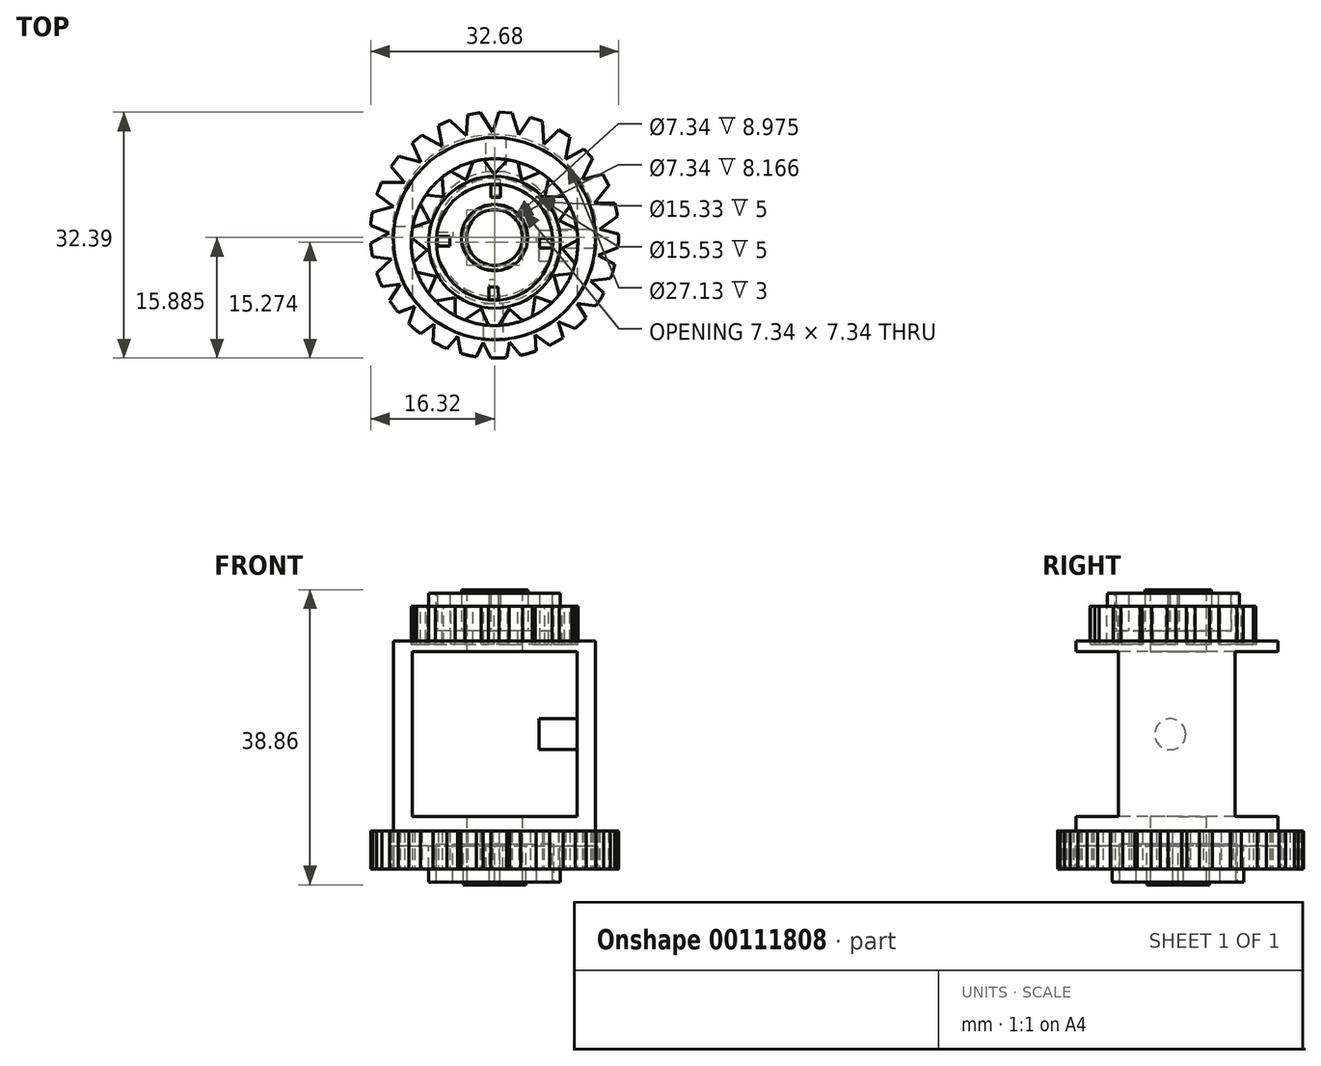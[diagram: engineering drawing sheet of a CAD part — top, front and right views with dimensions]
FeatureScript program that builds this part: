
annotation { "Feature Type Name" : "Feature", "Feature Type Description" : "" }
export const myFeature = defineFeature(function(context is Context, id is Id, definition is map)
    precondition{}
    {
        {
            var Q0;
            Q0=qCreatedBy(makeId("Top.planeOp"),FACE);
            var sketch = newSketch(context, id + "F0", { "sketchPlane" : qUnion([Q0])});
            skCircle(sketch, "E0", {"center": v(0, -2.17) * mm, "radius": 16.36 * mm});
            skSolve(sketch);
        }
        {
            var Q0;
            Q0=makeQuery(id+"F0.imprint","IMPRINT",FACE,{"disambiguationData":[TD([[makeQuery(id+"F0.imprint","IMPRINT",EDGE,{"derivedFrom":sQuery(id+"F0.wireOp",EDGE,"E0")}),1.0]])]});
            extrude(context, id + "F1", {"entities" : qUnion([Q0]), "oppositeDirection" : true, "depth" : 5 * mm});
        }
        {
            var Q0;
            Q0=qCreatedBy(makeId("Top.planeOp"),FACE);
            var sketch = newSketch(context, id + "F2", { "sketchPlane" : qUnion([Q0])});
            skCircle(sketch, "E1", {"center": v(0, -2.82) * mm, "radius": 13.3 * mm});
            skSolve(sketch);
        }
        {
            var Q0;
            Q0=makeQuery(id+"F2.imprint","IMPRINT",FACE,{"disambiguationData":[TD([[makeQuery(id+"F2.imprint","IMPRINT",EDGE,{"derivedFrom":sQuery(id+"F2.wireOp",EDGE,"E1")}),1.0]])]});
            extrude(context, id + "F3", {"entities" : qUnion([Q0]), "operationType" : NewBodyOperationType.ADD, "depth" : 25 * mm});
        }
        {
            var Q0;
            Q0=qCreatedBy(makeId("Top.planeOp"),FACE);
            var sketch = newSketch(context, id + "F4", { "sketchPlane" : qUnion([Q0])});
            skCircle(sketch, "E2", {"center": v(0, -3.26) * mm, "radius": 10.98 * mm});
            skSolve(sketch);
        }
        {
            var Q0;
            Q0 = qSketchRegion(id + "F4", true);
            extrude(context, id + "F5", {"entities" : qUnion([Q0]), "operationType" : NewBodyOperationType.ADD, "depth" : 29.59 * mm});
        }
        {
            var Q0;
            Q0=qCreatedBy(makeId("Front.planeOp"),FACE);
            var sketch = newSketch(context, id + "F6", { "sketchPlane" : qUnion([Q0])});
            skCircle(sketch, "E3.cCircle", {"center": v(0, 12.73) * mm, "radius": 10.86 * mm, "construction": true});
            skLineSegment(sketch, "E3.0", {"start": v(-10.86, 1.87) * mm, "end": v(-10.86, 23.59) * mm});
            skLineSegment(sketch, "E3.1", {"start": v(-10.86, 23.59) * mm, "end": v(10.86, 23.59) * mm});
            skLineSegment(sketch, "E3.2", {"start": v(10.86, 23.59) * mm, "end": v(10.86, 1.87) * mm});
            skLineSegment(sketch, "E3.3", {"start": v(10.86, 1.87) * mm, "end": v(-10.86, 1.87) * mm});
            skPoint(sketch, "E3.0.midPoint", {"position": v(-10.86, 12.73) * mm});
            skSolve(sketch);
        }
        {
            var Q0;
            Q0 = qSketchRegion(id + "F6", true);
            extrude(context, id + "F7", {"entities" : qUnion([Q0]), "operationType" : NewBodyOperationType.REMOVE, "oppositeDirection" : true, "depth" : 25 * mm});
        }
        {
            var Q0;
            Q0 = qSketchRegion(id + "F6", true);
            extrude(context, id + "F8", {"entities" : qUnion([Q0]), "operationType" : NewBodyOperationType.REMOVE, "depth" : 25.34 * mm});
        }
        {
            var Q0;
            Q0=qCreatedBy(makeId("Top.planeOp"),FACE);
            var sketch = newSketch(context, id + "F9", { "sketchPlane" : qUnion([Q0])});
            skCircle(sketch, "E4", {"center": v(0, -2.64) * mm, "radius": 3.67 * mm});
            skSolve(sketch);
        }
        {
            var Q0;
            Q0 = qSketchRegion(id + "F9", true);
            extrude(context, id + "F10", {"entities" : qUnion([Q0]), "operationType" : NewBodyOperationType.REMOVE, "depth" : 40.28 * mm});
        }
        {
            var Q0;
            Q0 = qSketchRegion(id + "F9", true);
            extrude(context, id + "F11", {"entities" : qUnion([Q0]), "operationType" : NewBodyOperationType.REMOVE, "oppositeDirection" : true, "depth" : 25 * mm});
        }
        {
            var Q0;
            Q0=makeQuery(id+"F5.opExtrude","CAP_FACE",FACE,{"disambiguationData":[OSD([sQuery(id+"F4.wireOp",EDGE,"E2")])],"isStart":false});
            var sketch = newSketch(context, id + "F12", { "sketchPlane" : qUnion([Q0])});
            skCircle(sketch, "E5", {"center": v(0, -3.26) * mm, "radius": 8.68 * mm});
            skSolve(sketch);
        }
        {
            var Q0;
            Q0=makeQuery(id+"F12.imprint","IMPRINT",FACE,{"disambiguationData":[TD([[makeQuery(id+"F12.imprint","IMPRINT",EDGE,{"derivedFrom":sQuery(id+"F12.wireOp",EDGE,"E5")}),1.0]])]});
            var sketch = newSketch(context, id + "F13", { "sketchPlane" : qUnion([Q0])});
            skCircle(sketch, "E6", {"center": v(0, -2.72) * mm, "radius": 3.88 * mm});
            skSolve(sketch);
        }
        {
            var Q0;
            Q0 = qSketchRegion(id + "F13", true);
            var Q1;
            Q1=makeQuery(id+"F12.imprint","IMPRINT",FACE,{"disambiguationData":[TD([[makeQuery(id+"F12.imprint","IMPRINT",EDGE,{"derivedFrom":sQuery(id+"F12.wireOp",EDGE,"E5")}),1.0]])]});
            extrude(context, id + "F14", {"entities" : qUnion([Q0, Q1]), "operationType" : NewBodyOperationType.ADD, "depth" : 1.74 * mm});
        }
        {
            var Q0;
            Q0=makeQuery(id+"F14.boolean.opBoolean","MERGE",FACE,{"derivedFrom":[makeQuery(id+"F14.opExtrude","CAP_FACE",FACE,{"disambiguationData":[OSD([sQuery(id+"F4.wireOp",EDGE,"E2"),sQuery(id+"F9.wireOp",EDGE,"E4"),sQuery(id+"F12.wireOp",EDGE,"E5")])],"isStart":false}),makeQuery(id+"F14.opExtrude","CAP_FACE",FACE,{"disambiguationData":[OSD([sQuery(id+"F13.wireOp",EDGE,"E6")])],"isStart":false})]});
            var sketch = newSketch(context, id + "F15", { "sketchPlane" : qUnion([Q0])});
            skCircle(sketch, "E7", {"center": v(0, -3.26) * mm, "radius": 7.67 * mm});
            skSolve(sketch);
        }
        {
            var Q0;
            Q0 = qSketchRegion(id + "F15", true);
            extrude(context, id + "F16", {"entities" : qUnion([Q0]), "operationType" : NewBodyOperationType.REMOVE, "oppositeDirection" : true, "depth" : 5 * mm});
        }
        {
            var Q0;
            Q0=makeQuery(id+"F16.boolean.opBoolean","COPY",FACE,{"derivedFrom":makeQuery(id+"F16.opExtrude","CAP_FACE",FACE,{"disambiguationData":[OSD([sQuery(id+"F15.wireOp",EDGE,"E7")])],"isStart":false})});
            var sketch = newSketch(context, id + "F17", { "sketchPlane" : qUnion([Q0])});
            skCircle(sketch, "E8", {"center": v(0, -2.64) * mm, "radius": 4.38 * mm});
            skSolve(sketch);
        }
        {
            var Q0;
            Q0 = qSketchRegion(id + "F17", true);
            extrude(context, id + "F18", {"entities" : qUnion([Q0]), "operationType" : NewBodyOperationType.ADD, "depth" : 5.43 * mm});
        }
        {
            var Q0;
            Q0 = qSketchRegion(id + "F9", true);
            extrude(context, id + "F19", {"entities" : qUnion([Q0]), "operationType" : NewBodyOperationType.REMOVE, "depth" : 40.72 * mm});
        }
        {
            var Q0;
            Q0=makeQuery(id+"F5.opExtrude","CAP_FACE",FACE,{"disambiguationData":[OSD([sQuery(id+"F4.wireOp",EDGE,"E2")])],"isStart":false});
            var sketch = newSketch(context, id + "F20", { "sketchPlane" : qUnion([Q0])});
            skLineSegment(sketch, "E9", {"start": v(-5.2, -10.2) * mm, "end": v(-5.2, -12.92) * mm});
            skLineSegment(sketch, "E10", {"start": v(-5.2, -12.92) * mm, "end": v(-3.94, -13.5) * mm});
            skLineSegment(sketch, "E11", {"start": v(-3.94, -13.5) * mm, "end": v(-1.46, -11.81) * mm});
            skLineSegment(sketch, "E12", {"start": v(-5.2, -10.2) * mm, "end": v(-1.46, -11.81) * mm});
            skLineSegment(sketch, "E13.1.0", {"start": v(-0.82, -14.2) * mm, "end": v(0.57, -14.22) * mm});
            skLineSegment(sketch, "E13.1.1", {"start": v(-1.93, -11.72) * mm, "end": v(-0.82, -14.2) * mm});
            skLineSegment(sketch, "E13.1.2", {"start": v(-1.93, -11.72) * mm, "end": v(2.14, -11.67) * mm});
            skLineSegment(sketch, "E13.1.3", {"start": v(0.57, -14.22) * mm, "end": v(2.14, -11.67) * mm});
            skLineSegment(sketch, "E13.2.0", {"start": v(3.7, -13.6) * mm, "end": v(4.98, -13.04) * mm});
            skLineSegment(sketch, "E13.2.1", {"start": v(1.68, -11.77) * mm, "end": v(3.7, -13.6) * mm});
            skLineSegment(sketch, "E13.2.2", {"start": v(1.68, -11.77) * mm, "end": v(5.38, -10.07) * mm});
            skLineSegment(sketch, "E13.2.3", {"start": v(4.98, -13.04) * mm, "end": v(5.38, -10.07) * mm});
            skLineSegment(sketch, "E13.3.0", {"start": v(7.59, -11.2) * mm, "end": v(8.53, -10.17) * mm});
            skLineSegment(sketch, "E13.3.1", {"start": v(5, -10.35) * mm, "end": v(7.59, -11.2) * mm});
            skLineSegment(sketch, "E13.3.2", {"start": v(5, -10.35) * mm, "end": v(7.69, -7.29) * mm});
            skLineSegment(sketch, "E13.3.3", {"start": v(8.53, -10.17) * mm, "end": v(7.69, -7.29) * mm});
            skLineSegment(sketch, "E13.4.0", {"start": v(10.16, -7.42) * mm, "end": v(10.6, -6.1) * mm});
            skLineSegment(sketch, "E13.4.1", {"start": v(7.45, -7.7) * mm, "end": v(10.16, -7.42) * mm});
            skLineSegment(sketch, "E13.4.2", {"start": v(7.45, -7.7) * mm, "end": v(8.66, -3.82) * mm});
            skLineSegment(sketch, "E13.4.3", {"start": v(10.6, -6.1) * mm, "end": v(8.66, -3.82) * mm});
            skLineSegment(sketch, "E13.5.0", {"start": v(10.97, -2.93) * mm, "end": v(10.85, -1.55) * mm});
            skLineSegment(sketch, "E13.5.1", {"start": v(8.62, -4.29) * mm, "end": v(10.97, -2.93) * mm});
            skLineSegment(sketch, "E13.5.2", {"start": v(8.62, -4.29) * mm, "end": v(8.14, -0.24) * mm});
            skLineSegment(sketch, "E13.5.3", {"start": v(10.85, -1.55) * mm, "end": v(8.14, -0.24) * mm});
            skLineSegment(sketch, "E13.6.0", {"start": v(9.9, 1.5) * mm, "end": v(9.21, 2.72) * mm});
            skLineSegment(sketch, "E13.6.1", {"start": v(8.3, -0.7) * mm, "end": v(9.9, 1.5) * mm});
            skLineSegment(sketch, "E13.6.2", {"start": v(8.3, -0.7) * mm, "end": v(6.21, 2.8) * mm});
            skLineSegment(sketch, "E13.6.3", {"start": v(9.21, 2.72) * mm, "end": v(6.21, 2.8) * mm});
            skLineSegment(sketch, "E13.7.0", {"start": v(7.1, 5.12) * mm, "end": v(5.99, 5.95) * mm});
            skLineSegment(sketch, "E13.7.1", {"start": v(6.53, 2.46) * mm, "end": v(7.1, 5.12) * mm});
            skLineSegment(sketch, "E13.7.2", {"start": v(6.53, 2.46) * mm, "end": v(3.2, 4.8) * mm});
            skLineSegment(sketch, "E13.7.3", {"start": v(5.99, 5.95) * mm, "end": v(3.2, 4.8) * mm});
            skLineSegment(sketch, "E13.8.0", {"start": v(3.08, 7.28) * mm, "end": v(1.73, 7.59) * mm});
            skLineSegment(sketch, "E13.8.1", {"start": v(3.65, 4.62) * mm, "end": v(3.08, 7.28) * mm});
            skLineSegment(sketch, "E13.8.2", {"start": v(3.65, 4.62) * mm, "end": v(-0.35, 5.42) * mm});
            skLineSegment(sketch, "E13.8.3", {"start": v(1.73, 7.59) * mm, "end": v(-0.35, 5.42) * mm});
            skLineSegment(sketch, "E13.9.0", {"start": v(-1.47, 7.62) * mm, "end": v(-2.83, 7.35) * mm});
            skLineSegment(sketch, "E13.9.1", {"start": v(0.13, 5.42) * mm, "end": v(-1.47, 7.62) * mm});
            skLineSegment(sketch, "E13.9.2", {"start": v(0.13, 5.42) * mm, "end": v(-3.85, 4.53) * mm});
            skLineSegment(sketch, "E13.9.3", {"start": v(-2.83, 7.35) * mm, "end": v(-3.85, 4.53) * mm});
            skLineSegment(sketch, "E13.10.0", {"start": v(-5.77, 6.08) * mm, "end": v(-6.9, 5.28) * mm});
            skLineSegment(sketch, "E13.10.1", {"start": v(-3.41, 4.72) * mm, "end": v(-5.77, 6.08) * mm});
            skLineSegment(sketch, "E13.10.2", {"start": v(-3.41, 4.72) * mm, "end": v(-6.68, 2.29) * mm});
            skLineSegment(sketch, "E13.10.3", {"start": v(-6.9, 5.28) * mm, "end": v(-6.68, 2.29) * mm});
            skLineSegment(sketch, "E13.11.0", {"start": v(-9.07, 2.93) * mm, "end": v(-9.78, 1.74) * mm});
            skLineSegment(sketch, "E13.11.1", {"start": v(-6.36, 2.65) * mm, "end": v(-9.07, 2.93) * mm});
            skLineSegment(sketch, "E13.11.2", {"start": v(-6.36, 2.65) * mm, "end": v(-8.36, -0.9) * mm});
            skLineSegment(sketch, "E13.11.3", {"start": v(-9.78, 1.74) * mm, "end": v(-8.36, -0.9) * mm});
            skLineSegment(sketch, "E13.12.0", {"start": v(-10.8, -1.3) * mm, "end": v(-10.96, -2.67) * mm});
            skLineSegment(sketch, "E13.12.1", {"start": v(-8.21, -0.45) * mm, "end": v(-10.8, -1.3) * mm});
            skLineSegment(sketch, "E13.12.2", {"start": v(-8.21, -0.45) * mm, "end": v(-8.59, -4.5) * mm});
            skLineSegment(sketch, "E13.12.3", {"start": v(-10.96, -2.67) * mm, "end": v(-8.59, -4.5) * mm});
            skLineSegment(sketch, "E13.13.0", {"start": v(-10.67, -5.86) * mm, "end": v(-10.25, -7.18) * mm});
            skLineSegment(sketch, "E13.13.1", {"start": v(-8.64, -4.04) * mm, "end": v(-10.67, -5.86) * mm});
            skLineSegment(sketch, "E13.13.2", {"start": v(-8.64, -4.04) * mm, "end": v(-7.34, -7.9) * mm});
            skLineSegment(sketch, "E13.13.3", {"start": v(-10.25, -7.18) * mm, "end": v(-7.34, -7.9) * mm});
            skLineSegment(sketch, "E13.14.0", {"start": v(-8.69, -9.97) * mm, "end": v(-7.77, -11.01) * mm});
            skLineSegment(sketch, "E13.14.1", {"start": v(-7.58, -7.49) * mm, "end": v(-8.69, -9.97) * mm});
            skLineSegment(sketch, "E13.14.2", {"start": v(-7.58, -7.49) * mm, "end": v(-4.82, -10.48) * mm});
            skLineSegment(sketch, "E13.14.3", {"start": v(-7.77, -11.01) * mm, "end": v(-4.82, -10.48) * mm});
            skPoint(sketch, "E13.center", {"position": v(0, -3.26) * mm});
            skSolve(sketch);
        }
        {
            var Q0;
            {var subQ0=sQuery(id+"F20.wireOp",EDGE,"E13.11.3");var subQ3=sQuery(id+"F20.wireOp",EDGE,"E13.12.1");var subQ4=makeQuery(id+"F20.imprint","INTERSECT",VERTEX,{"derivedFrom":[subQ0,subQ3]});Q0=makeQuery(id+"F20.imprint","IMPRINT",FACE,{"disambiguationData":[TD([[makeQuery(id+"F20.imprint","IMPRINT",EDGE,{"disambiguationData":[TD([[subQ4,1.0]])],"derivedFrom":subQ0}),-1.0]])]});}
            var Q1;
            {var subQ0=sQuery(id+"F20.wireOp",EDGE,"E13.12.3");var subQ3=sQuery(id+"F20.wireOp",EDGE,"E13.13.1");var subQ4=makeQuery(id+"F20.imprint","INTERSECT",VERTEX,{"derivedFrom":[subQ0,subQ3]});Q1=makeQuery(id+"F20.imprint","IMPRINT",FACE,{"disambiguationData":[TD([[makeQuery(id+"F20.imprint","IMPRINT",EDGE,{"disambiguationData":[TD([[subQ4,1.0]])],"derivedFrom":subQ0}),-1.0]])]});}
            var Q2;
            {var subQ0=sQuery(id+"F20.wireOp",EDGE,"E13.13.3");var subQ3=sQuery(id+"F20.wireOp",EDGE,"E13.14.1");var subQ4=makeQuery(id+"F20.imprint","INTERSECT",VERTEX,{"derivedFrom":[subQ0,subQ3]});Q2=makeQuery(id+"F20.imprint","IMPRINT",FACE,{"disambiguationData":[TD([[makeQuery(id+"F20.imprint","IMPRINT",EDGE,{"disambiguationData":[TD([[subQ4,1.0]])],"derivedFrom":subQ0}),-1.0]])]});}
            var Q3;
            {var subQ0=sQuery(id+"F20.wireOp",EDGE,"E11");var subQ3=sQuery(id+"F20.wireOp",EDGE,"E13.1.1");var subQ4=makeQuery(id+"F20.imprint","INTERSECT",VERTEX,{"derivedFrom":[subQ0,subQ3]});Q3=makeQuery(id+"F20.imprint","IMPRINT",FACE,{"disambiguationData":[TD([[makeQuery(id+"F20.imprint","IMPRINT",EDGE,{"disambiguationData":[TD([[subQ4,1.0]])],"derivedFrom":subQ0}),-1.0]])]});}
            var Q4;
            {var subQ0=sQuery(id+"F20.wireOp",EDGE,"E9");var subQ3=sQuery(id+"F20.wireOp",EDGE,"E13.14.3");var subQ4=makeQuery(id+"F20.imprint","INTERSECT",VERTEX,{"derivedFrom":[subQ0,subQ3]});Q4=makeQuery(id+"F20.imprint","IMPRINT",FACE,{"disambiguationData":[TD([[makeQuery(id+"F20.imprint","IMPRINT",EDGE,{"disambiguationData":[TD([[subQ4,-1.0]])],"derivedFrom":subQ0}),-1.0]])]});}
            var Q5;
            {var subQ0=sQuery(id+"F20.wireOp",EDGE,"E13.1.3");var subQ3=sQuery(id+"F20.wireOp",EDGE,"E13.2.1");var subQ4=makeQuery(id+"F20.imprint","INTERSECT",VERTEX,{"derivedFrom":[subQ0,subQ3]});Q5=makeQuery(id+"F20.imprint","IMPRINT",FACE,{"disambiguationData":[TD([[makeQuery(id+"F20.imprint","IMPRINT",EDGE,{"disambiguationData":[TD([[subQ4,1.0]])],"derivedFrom":subQ0}),-1.0]])]});}
            var Q6;
            {var subQ0=sQuery(id+"F20.wireOp",EDGE,"E13.2.3");var subQ3=sQuery(id+"F20.wireOp",EDGE,"E13.3.1");var subQ4=makeQuery(id+"F20.imprint","INTERSECT",VERTEX,{"derivedFrom":[subQ0,subQ3]});Q6=makeQuery(id+"F20.imprint","IMPRINT",FACE,{"disambiguationData":[TD([[makeQuery(id+"F20.imprint","IMPRINT",EDGE,{"disambiguationData":[TD([[subQ4,1.0]])],"derivedFrom":subQ0}),-1.0]])]});}
            var Q7;
            {var subQ0=sQuery(id+"F20.wireOp",EDGE,"E13.3.3");var subQ3=sQuery(id+"F20.wireOp",EDGE,"E13.4.1");var subQ4=makeQuery(id+"F20.imprint","INTERSECT",VERTEX,{"derivedFrom":[subQ0,subQ3]});Q7=makeQuery(id+"F20.imprint","IMPRINT",FACE,{"disambiguationData":[TD([[makeQuery(id+"F20.imprint","IMPRINT",EDGE,{"disambiguationData":[TD([[subQ4,1.0]])],"derivedFrom":subQ0}),-1.0]])]});}
            var Q8;
            {var subQ0=sQuery(id+"F20.wireOp",EDGE,"E13.4.3");var subQ3=sQuery(id+"F20.wireOp",EDGE,"E13.5.1");var subQ4=makeQuery(id+"F20.imprint","INTERSECT",VERTEX,{"derivedFrom":[subQ0,subQ3]});Q8=makeQuery(id+"F20.imprint","IMPRINT",FACE,{"disambiguationData":[TD([[makeQuery(id+"F20.imprint","IMPRINT",EDGE,{"disambiguationData":[TD([[subQ4,1.0]])],"derivedFrom":subQ0}),-1.0]])]});}
            var Q9;
            {var subQ0=sQuery(id+"F20.wireOp",EDGE,"E13.5.3");var subQ3=sQuery(id+"F20.wireOp",EDGE,"E13.6.1");var subQ4=makeQuery(id+"F20.imprint","INTERSECT",VERTEX,{"derivedFrom":[subQ0,subQ3]});Q9=makeQuery(id+"F20.imprint","IMPRINT",FACE,{"disambiguationData":[TD([[makeQuery(id+"F20.imprint","IMPRINT",EDGE,{"disambiguationData":[TD([[subQ4,1.0]])],"derivedFrom":subQ0}),-1.0]])]});}
            var Q10;
            {var subQ0=sQuery(id+"F20.wireOp",EDGE,"E13.6.3");var subQ3=sQuery(id+"F20.wireOp",EDGE,"E13.7.1");var subQ4=makeQuery(id+"F20.imprint","INTERSECT",VERTEX,{"derivedFrom":[subQ0,subQ3]});Q10=makeQuery(id+"F20.imprint","IMPRINT",FACE,{"disambiguationData":[TD([[makeQuery(id+"F20.imprint","IMPRINT",EDGE,{"disambiguationData":[TD([[subQ4,1.0]])],"derivedFrom":subQ0}),-1.0]])]});}
            var Q11;
            {var subQ0=sQuery(id+"F20.wireOp",EDGE,"E13.7.3");var subQ3=sQuery(id+"F20.wireOp",EDGE,"E13.8.1");var subQ4=makeQuery(id+"F20.imprint","INTERSECT",VERTEX,{"derivedFrom":[subQ0,subQ3]});Q11=makeQuery(id+"F20.imprint","IMPRINT",FACE,{"disambiguationData":[TD([[makeQuery(id+"F20.imprint","IMPRINT",EDGE,{"disambiguationData":[TD([[subQ4,1.0]])],"derivedFrom":subQ0}),-1.0]])]});}
            var Q12;
            {var subQ0=sQuery(id+"F20.wireOp",EDGE,"E13.8.3");var subQ3=sQuery(id+"F20.wireOp",EDGE,"E13.9.1");var subQ4=makeQuery(id+"F20.imprint","INTERSECT",VERTEX,{"derivedFrom":[subQ0,subQ3]});Q12=makeQuery(id+"F20.imprint","IMPRINT",FACE,{"disambiguationData":[TD([[makeQuery(id+"F20.imprint","IMPRINT",EDGE,{"disambiguationData":[TD([[subQ4,1.0]])],"derivedFrom":subQ0}),-1.0]])]});}
            var Q13;
            {var subQ0=sQuery(id+"F20.wireOp",EDGE,"E13.9.3");var subQ3=sQuery(id+"F20.wireOp",EDGE,"E13.10.1");var subQ4=makeQuery(id+"F20.imprint","INTERSECT",VERTEX,{"derivedFrom":[subQ0,subQ3]});Q13=makeQuery(id+"F20.imprint","IMPRINT",FACE,{"disambiguationData":[TD([[makeQuery(id+"F20.imprint","IMPRINT",EDGE,{"disambiguationData":[TD([[subQ4,1.0]])],"derivedFrom":subQ0}),-1.0]])]});}
            var Q14;
            {var subQ0=sQuery(id+"F20.wireOp",EDGE,"E13.10.3");var subQ3=sQuery(id+"F20.wireOp",EDGE,"E13.11.1");var subQ4=makeQuery(id+"F20.imprint","INTERSECT",VERTEX,{"derivedFrom":[subQ0,subQ3]});Q14=makeQuery(id+"F20.imprint","IMPRINT",FACE,{"disambiguationData":[TD([[makeQuery(id+"F20.imprint","IMPRINT",EDGE,{"disambiguationData":[TD([[subQ4,1.0]])],"derivedFrom":subQ0}),-1.0]])]});}
            extrude(context, id + "F21", {"entities" : qUnion([Q0, Q1, Q2, Q3, Q4, Q5, Q6, Q7, Q8, Q9, Q10, Q11, Q12, Q13, Q14]), "operationType" : NewBodyOperationType.REMOVE, "oppositeDirection" : true, "depth" : 5 * mm});
        }
        {
            var Q0;
            Q0=makeQuery(id+"F1.opExtrude","CAP_FACE",FACE,{"disambiguationData":[OSD([sQuery(id+"F0.wireOp",EDGE,"E0")])],"isStart":false});
            var sketch = newSketch(context, id + "F22", { "sketchPlane" : qUnion([Q0])});
            skCircle(sketch, "E14", {"center": v(0, 2.64) * mm, "radius": 8.67 * mm});
            skSolve(sketch);
        }
        {
            var Q0;
            Q0 = qSketchRegion(id + "F22", true);
            extrude(context, id + "F23", {"entities" : qUnion([Q0]), "operationType" : NewBodyOperationType.ADD, "depth" : 1.75 * mm});
        }
        {
            var Q0;
            Q0=makeQuery(id+"F23.opExtrude","CAP_FACE",FACE,{"disambiguationData":[OSD([sQuery(id+"F22.wireOp",EDGE,"E14")])],"isStart":false});
            var sketch = newSketch(context, id + "F24", { "sketchPlane" : qUnion([Q0])});
            skCircle(sketch, "E15", {"center": v(0, 2.64) * mm, "radius": 7.76 * mm});
            skSolve(sketch);
        }
        {
            var Q0;
            Q0=makeQuery(id+"F24.imprint","IMPRINT",FACE,{"disambiguationData":[TD([[makeQuery(id+"F24.imprint","IMPRINT",EDGE,{"derivedFrom":sQuery(id+"F24.wireOp",EDGE,"E15")}),1.0]])]});
            extrude(context, id + "F25", {"entities" : qUnion([Q0]), "operationType" : NewBodyOperationType.REMOVE, "oppositeDirection" : true, "depth" : 5 * mm});
        }
        {
            var Q0;
            Q0=makeQuery(id+"F25.boolean.opBoolean","COPY",FACE,{"derivedFrom":makeQuery(id+"F25.opExtrude","CAP_FACE",FACE,{"disambiguationData":[OSD([sQuery(id+"F24.wireOp",EDGE,"E15")])],"isStart":false})});
            var sketch = newSketch(context, id + "F26", { "sketchPlane" : qUnion([Q0])});
            skCircle(sketch, "E16", {"center": v(0, 2.64) * mm, "radius": 4.13 * mm});
            skSolve(sketch);
        }
        {
            var Q0;
            Q0 = qSketchRegion(id + "F26", true);
            extrude(context, id + "F27", {"entities" : qUnion([Q0]), "operationType" : NewBodyOperationType.ADD, "depth" : 5.36 * mm});
        }
        {
            var Q0;
            Q0 = qSketchRegion(id + "F9", true);
            extrude(context, id + "F28", {"entities" : qUnion([Q0]), "operationType" : NewBodyOperationType.REMOVE, "oppositeDirection" : true, "depth" : 25 * mm});
        }
        {
            var Q0;
            Q0=makeQuery(id+"F1.opExtrude","CAP_FACE",FACE,{"disambiguationData":[OSD([sQuery(id+"F0.wireOp",EDGE,"E0")])],"isStart":false});
            var sketch = newSketch(context, id + "F29", { "sketchPlane" : qUnion([Q0])});
            skCircle(sketch, "E17", {"center": v(0, 2.64) * mm, "radius": 13.56 * mm});
            skSolve(sketch);
        }
        {
            var Q0;
            Q0=makeQuery(id+"F29.imprint","IMPRINT",FACE,{"disambiguationData":[TD([[makeQuery(id+"F29.imprint","IMPRINT",EDGE,{"derivedFrom":sQuery(id+"F29.wireOp",EDGE,"E17")}),1.0]])]});
            extrude(context, id + "F30", {"entities" : qUnion([Q0]), "operationType" : NewBodyOperationType.REMOVE, "oppositeDirection" : true, "depth" : 3 * mm});
        }
        {
            var Q0;
            Q0=makeQuery(id+"F1.opExtrude","CAP_FACE",FACE,{"disambiguationData":[OSD([sQuery(id+"F0.wireOp",EDGE,"E0")])],"isStart":false});
            var sketch = newSketch(context, id + "F31", { "sketchPlane" : qUnion([Q0])});
            skLineSegment(sketch, "E18", {"start": v(-13, -1.2) * mm, "end": v(-11.48, -4.58) * mm});
            skLineSegment(sketch, "E19", {"start": v(-11.48, -4.58) * mm, "end": v(-14.9, -4.58) * mm});
            skLineSegment(sketch, "E20", {"start": v(-14.9, -4.58) * mm, "end": v(-15.5, -3.03) * mm});
            skLineSegment(sketch, "E21", {"start": v(-15.5, -3.03) * mm, "end": v(-13, -1.2) * mm});
            skLineSegment(sketch, "E22.1.0", {"start": v(-9.32, -7.21) * mm, "end": v(-12.63, -8.06) * mm});
            skLineSegment(sketch, "E22.1.1", {"start": v(-11.64, -4.31) * mm, "end": v(-9.32, -7.21) * mm});
            skLineSegment(sketch, "E22.1.2", {"start": v(-13.6, -6.7) * mm, "end": v(-11.64, -4.31) * mm});
            skLineSegment(sketch, "E22.1.3", {"start": v(-12.63, -8.06) * mm, "end": v(-13.6, -6.7) * mm});
            skLineSegment(sketch, "E22.2.0", {"start": v(-6.58, -9.22) * mm, "end": v(-9.57, -10.86) * mm});
            skLineSegment(sketch, "E22.2.1", {"start": v(-9.55, -6.99) * mm, "end": v(-6.58, -9.22) * mm});
            skLineSegment(sketch, "E22.2.2", {"start": v(-10.85, -9.8) * mm, "end": v(-9.55, -6.99) * mm});
            skLineSegment(sketch, "E22.2.3", {"start": v(-9.57, -10.86) * mm, "end": v(-10.85, -9.8) * mm});
            skLineSegment(sketch, "E22.3.0", {"start": v(-3.42, -10.48) * mm, "end": v(-5.91, -12.82) * mm});
            skLineSegment(sketch, "E22.3.1", {"start": v(-6.85, -9.06) * mm, "end": v(-3.42, -10.48) * mm});
            skLineSegment(sketch, "E22.3.2", {"start": v(-7.42, -12.1) * mm, "end": v(-6.85, -9.06) * mm});
            skLineSegment(sketch, "E22.3.3", {"start": v(-5.91, -12.82) * mm, "end": v(-7.42, -12.1) * mm});
            skLineSegment(sketch, "E22.4.0", {"start": v(-0.05, -10.92) * mm, "end": v(-1.88, -13.8) * mm});
            skLineSegment(sketch, "E22.4.1", {"start": v(-3.73, -10.4) * mm, "end": v(-0.05, -10.92) * mm});
            skLineSegment(sketch, "E22.4.2", {"start": v(-3.52, -13.49) * mm, "end": v(-3.73, -10.4) * mm});
            skLineSegment(sketch, "E22.4.3", {"start": v(-1.88, -13.8) * mm, "end": v(-3.52, -13.49) * mm});
            skLineSegment(sketch, "E22.5.0", {"start": v(3.33, -10.5) * mm, "end": v(2.27, -13.76) * mm});
            skLineSegment(sketch, "E22.5.1", {"start": v(-0.36, -10.91) * mm, "end": v(3.33, -10.5) * mm});
            skLineSegment(sketch, "E22.5.2", {"start": v(0.6, -13.86) * mm, "end": v(-0.36, -10.91) * mm});
            skLineSegment(sketch, "E22.5.3", {"start": v(2.27, -13.76) * mm, "end": v(0.6, -13.86) * mm});
            skLineSegment(sketch, "E22.6.0", {"start": v(6.5, -9.26) * mm, "end": v(6.28, -12.68) * mm});
            skLineSegment(sketch, "E22.6.1", {"start": v(3.02, -10.58) * mm, "end": v(6.5, -9.26) * mm});
            skLineSegment(sketch, "E22.6.2", {"start": v(4.7, -13.19) * mm, "end": v(3.02, -10.58) * mm});
            skLineSegment(sketch, "E22.6.3", {"start": v(6.28, -12.68) * mm, "end": v(4.7, -13.19) * mm});
            skLineSegment(sketch, "E22.7.0", {"start": v(9.25, -7.28) * mm, "end": v(9.9, -10.63) * mm});
            skLineSegment(sketch, "E22.7.1", {"start": v(6.21, -9.41) * mm, "end": v(9.25, -7.28) * mm});
            skLineSegment(sketch, "E22.7.2", {"start": v(8.48, -11.52) * mm, "end": v(6.21, -9.41) * mm});
            skLineSegment(sketch, "E22.7.3", {"start": v(9.9, -10.63) * mm, "end": v(8.48, -11.52) * mm});
            skLineSegment(sketch, "E22.8.0", {"start": v(11.43, -4.66) * mm, "end": v(12.88, -7.76) * mm});
            skLineSegment(sketch, "E22.8.1", {"start": v(9.02, -7.49) * mm, "end": v(11.43, -4.66) * mm});
            skLineSegment(sketch, "E22.8.2", {"start": v(11.74, -8.97) * mm, "end": v(9.02, -7.49) * mm});
            skLineSegment(sketch, "E22.8.3", {"start": v(12.88, -7.76) * mm, "end": v(11.74, -8.97) * mm});
            skLineSegment(sketch, "E22.9.0", {"start": v(12.89, -1.6) * mm, "end": v(15.06, -4.23) * mm});
            skLineSegment(sketch, "E22.9.1", {"start": v(11.25, -4.93) * mm, "end": v(12.89, -1.6) * mm});
            skLineSegment(sketch, "E22.9.2", {"start": v(14.26, -5.68) * mm, "end": v(11.25, -4.93) * mm});
            skLineSegment(sketch, "E22.9.3", {"start": v(15.06, -4.23) * mm, "end": v(14.26, -5.68) * mm});
            skLineSegment(sketch, "E22.10.0", {"start": v(13.53, 1.75) * mm, "end": v(16.3, -0.26) * mm});
            skLineSegment(sketch, "E22.10.1", {"start": v(12.78, -1.9) * mm, "end": v(13.53, 1.75) * mm});
            skLineSegment(sketch, "E22.10.2", {"start": v(15.88, -1.88) * mm, "end": v(12.78, -1.9) * mm});
            skLineSegment(sketch, "E22.10.3", {"start": v(16.3, -0.26) * mm, "end": v(15.88, -1.88) * mm});
            skLineSegment(sketch, "E22.11.0", {"start": v(13.33, 5.14) * mm, "end": v(16.51, 3.88) * mm});
            skLineSegment(sketch, "E22.11.1", {"start": v(13.5, 1.43) * mm, "end": v(13.33, 5.14) * mm});
            skLineSegment(sketch, "E22.11.2", {"start": v(16.5, 2.21) * mm, "end": v(13.5, 1.43) * mm});
            skLineSegment(sketch, "E22.11.3", {"start": v(16.51, 3.88) * mm, "end": v(16.5, 2.21) * mm});
            skLineSegment(sketch, "E22.12.0", {"start": v(12.3, 8.38) * mm, "end": v(15.68, 7.95) * mm});
            skLineSegment(sketch, "E22.12.1", {"start": v(13.39, 4.83) * mm, "end": v(12.3, 8.38) * mm});
            skLineSegment(sketch, "E22.12.2", {"start": v(16.1, 6.33) * mm, "end": v(13.39, 4.83) * mm});
            skLineSegment(sketch, "E22.12.3", {"start": v(15.68, 7.95) * mm, "end": v(16.1, 6.33) * mm});
            skLineSegment(sketch, "E22.13.0", {"start": v(10.48, 11.25) * mm, "end": v(13.87, 11.68) * mm});
            skLineSegment(sketch, "E22.13.1", {"start": v(12.42, 8.09) * mm, "end": v(10.48, 11.25) * mm});
            skLineSegment(sketch, "E22.13.2", {"start": v(14.67, 10.22) * mm, "end": v(12.42, 8.09) * mm});
            skLineSegment(sketch, "E22.13.3", {"start": v(13.87, 11.68) * mm, "end": v(14.67, 10.22) * mm});
            skLineSegment(sketch, "E22.14.0", {"start": v(8.01, 13.6) * mm, "end": v(11.19, 14.85) * mm});
            skLineSegment(sketch, "E22.14.1", {"start": v(10.68, 11) * mm, "end": v(8.01, 13.6) * mm});
            skLineSegment(sketch, "E22.14.2", {"start": v(12.33, 13.63) * mm, "end": v(10.68, 11) * mm});
            skLineSegment(sketch, "E22.14.3", {"start": v(11.19, 14.85) * mm, "end": v(12.33, 13.63) * mm});
            skLineSegment(sketch, "E22.15.0", {"start": v(5.04, 15.24) * mm, "end": v(7.8, 17.25) * mm});
            skLineSegment(sketch, "E22.15.1", {"start": v(8.26, 13.4) * mm, "end": v(5.04, 15.24) * mm});
            skLineSegment(sketch, "E22.15.2", {"start": v(9.2, 16.35) * mm, "end": v(8.26, 13.4) * mm});
            skLineSegment(sketch, "E22.15.3", {"start": v(7.8, 17.25) * mm, "end": v(9.2, 16.35) * mm});
            skLineSegment(sketch, "E22.16.0", {"start": v(1.75, 16.1) * mm, "end": v(3.93, 18.73) * mm});
            skLineSegment(sketch, "E22.16.1", {"start": v(5.33, 15.12) * mm, "end": v(1.75, 16.1) * mm});
            skLineSegment(sketch, "E22.16.2", {"start": v(5.51, 18.21) * mm, "end": v(5.33, 15.12) * mm});
            skLineSegment(sketch, "E22.16.3", {"start": v(3.93, 18.73) * mm, "end": v(5.51, 18.21) * mm});
            skLineSegment(sketch, "E22.17.0", {"start": v(-1.65, 16.1) * mm, "end": v(-0.2, 19.2) * mm});
            skLineSegment(sketch, "E22.17.1", {"start": v(2.06, 16.05) * mm, "end": v(-1.65, 16.1) * mm});
            skLineSegment(sketch, "E22.17.2", {"start": v(1.47, 19.1) * mm, "end": v(2.06, 16.05) * mm});
            skLineSegment(sketch, "E22.17.3", {"start": v(-0.2, 19.2) * mm, "end": v(1.47, 19.1) * mm});
            skLineSegment(sketch, "E22.18.0", {"start": v(-4.95, 15.27) * mm, "end": v(-4.3, 18.63) * mm});
            skLineSegment(sketch, "E22.18.1", {"start": v(-1.34, 16.14) * mm, "end": v(-4.95, 15.27) * mm});
            skLineSegment(sketch, "E22.18.2", {"start": v(-2.67, 18.94) * mm, "end": v(-1.34, 16.14) * mm});
            skLineSegment(sketch, "E22.18.3", {"start": v(-4.3, 18.63) * mm, "end": v(-2.67, 18.94) * mm});
            skLineSegment(sketch, "E22.19.0", {"start": v(-7.93, 13.65) * mm, "end": v(-8.15, 17.06) * mm});
            skLineSegment(sketch, "E22.19.1", {"start": v(-4.65, 15.39) * mm, "end": v(-7.93, 13.65) * mm});
            skLineSegment(sketch, "E22.19.2", {"start": v(-6.64, 17.76) * mm, "end": v(-4.65, 15.39) * mm});
            skLineSegment(sketch, "E22.19.3", {"start": v(-8.15, 17.06) * mm, "end": v(-6.64, 17.76) * mm});
            skLineSegment(sketch, "E22.20.0", {"start": v(-10.42, 11.33) * mm, "end": v(-11.48, 14.58) * mm});
            skLineSegment(sketch, "E22.20.1", {"start": v(-7.67, 13.83) * mm, "end": v(-10.42, 11.33) * mm});
            skLineSegment(sketch, "E22.20.2", {"start": v(-10.19, 15.64) * mm, "end": v(-7.67, 13.83) * mm});
            skLineSegment(sketch, "E22.20.3", {"start": v(-11.48, 14.58) * mm, "end": v(-10.19, 15.64) * mm});
            skLineSegment(sketch, "E22.21.0", {"start": v(-12.25, 8.46) * mm, "end": v(-14.08, 11.35) * mm});
            skLineSegment(sketch, "E22.21.1", {"start": v(-10.21, 11.57) * mm, "end": v(-12.25, 8.46) * mm});
            skLineSegment(sketch, "E22.21.2", {"start": v(-13.1, 12.7) * mm, "end": v(-10.21, 11.57) * mm});
            skLineSegment(sketch, "E22.21.3", {"start": v(-14.08, 11.35) * mm, "end": v(-13.1, 12.7) * mm});
            skLineSegment(sketch, "E22.22.0", {"start": v(-13.31, 5.23) * mm, "end": v(-15.8, 7.57) * mm});
            skLineSegment(sketch, "E22.22.1", {"start": v(-12.11, 8.75) * mm, "end": v(-13.31, 5.23) * mm});
            skLineSegment(sketch, "E22.22.2", {"start": v(-15.19, 9.12) * mm, "end": v(-12.11, 8.75) * mm});
            skLineSegment(sketch, "E22.22.3", {"start": v(-15.8, 7.57) * mm, "end": v(-15.19, 9.12) * mm});
            skLineSegment(sketch, "E22.23.0", {"start": v(-13.54, 1.84) * mm, "end": v(-16.53, 3.49) * mm});
            skLineSegment(sketch, "E22.23.1", {"start": v(-13.25, 5.54) * mm, "end": v(-13.54, 1.84) * mm});
            skLineSegment(sketch, "E22.23.2", {"start": v(-16.32, 5.14) * mm, "end": v(-13.25, 5.54) * mm});
            skLineSegment(sketch, "E22.23.3", {"start": v(-16.53, 3.49) * mm, "end": v(-16.32, 5.14) * mm});
            skLineSegment(sketch, "E22.24.0", {"start": v(-12.91, -1.5) * mm, "end": v(-16.22, -0.65) * mm});
            skLineSegment(sketch, "E22.24.1", {"start": v(-13.55, 2.16) * mm, "end": v(-12.91, -1.5) * mm});
            skLineSegment(sketch, "E22.24.2", {"start": v(-16.43, 1) * mm, "end": v(-13.55, 2.16) * mm});
            skLineSegment(sketch, "E22.24.3", {"start": v(-16.22, -0.65) * mm, "end": v(-16.43, 1) * mm});
            skPoint(sketch, "E22.center", {"position": v(0, 2.64) * mm});
            skSolve(sketch);
        }
        {
            var Q0;
            {var subQ0=sQuery(id+"F31.wireOp",EDGE,"E22.24.2");var subQ1=sQuery(id+"F31.wireOp",EDGE,"E22.23.0");var subQ2=makeQuery(id+"F31.imprint","INTERSECT",VERTEX,{"derivedFrom":[subQ1,subQ0]});Q0=makeQuery(id+"F31.imprint","IMPRINT",FACE,{"disambiguationData":[TD([[makeQuery(id+"F31.imprint","IMPRINT",EDGE,{"disambiguationData":[TD([[subQ2,-1.0]])],"derivedFrom":subQ1}),1.0]])]});}
            var Q1;
            {var subQ0=sQuery(id+"F31.wireOp",EDGE,"E21");var subQ3=sQuery(id+"F31.wireOp",EDGE,"E22.24.0");var subQ4=makeQuery(id+"F31.imprint","INTERSECT",VERTEX,{"derivedFrom":[subQ0,subQ3]});Q1=makeQuery(id+"F31.imprint","IMPRINT",FACE,{"disambiguationData":[TD([[makeQuery(id+"F31.imprint","IMPRINT",EDGE,{"disambiguationData":[TD([[subQ4,-1.0]])],"derivedFrom":subQ3}),1.0]])]});}
            var Q2;
            {var subQ14=sQuery(id+"F31.wireOp",EDGE,"E22.1.3");Q2=makeQuery(id+"F31.imprint","IMPRINT",FACE,{"disambiguationData":[TD([[makeQuery(id+"F31.imprint","IMPRINT",EDGE,{"derivedFrom":subQ14}),1.0]])]});}
            var Q3;
            {var subQ0=sQuery(id+"F31.wireOp",EDGE,"E22.10.2");var subQ1=sQuery(id+"F31.wireOp",EDGE,"E22.9.0");var subQ2=makeQuery(id+"F31.imprint","INTERSECT",VERTEX,{"derivedFrom":[subQ1,subQ0]});Q3=makeQuery(id+"F31.imprint","IMPRINT",FACE,{"disambiguationData":[TD([[makeQuery(id+"F31.imprint","IMPRINT",EDGE,{"disambiguationData":[TD([[subQ2,-1.0]])],"derivedFrom":subQ1}),1.0]])]});}
            var Q4;
            {var subQ0=sQuery(id+"F31.wireOp",EDGE,"E22.11.2");var subQ1=sQuery(id+"F31.wireOp",EDGE,"E22.10.0");var subQ2=makeQuery(id+"F31.imprint","INTERSECT",VERTEX,{"derivedFrom":[subQ1,subQ0]});Q4=makeQuery(id+"F31.imprint","IMPRINT",FACE,{"disambiguationData":[TD([[makeQuery(id+"F31.imprint","IMPRINT",EDGE,{"disambiguationData":[TD([[subQ2,-1.0]])],"derivedFrom":subQ1}),1.0]])]});}
            var Q5;
            {var subQ0=sQuery(id+"F31.wireOp",EDGE,"E22.12.2");var subQ1=sQuery(id+"F31.wireOp",EDGE,"E22.11.0");var subQ2=makeQuery(id+"F31.imprint","INTERSECT",VERTEX,{"derivedFrom":[subQ1,subQ0]});Q5=makeQuery(id+"F31.imprint","IMPRINT",FACE,{"disambiguationData":[TD([[makeQuery(id+"F31.imprint","IMPRINT",EDGE,{"disambiguationData":[TD([[subQ2,-1.0]])],"derivedFrom":subQ1}),1.0]])]});}
            var Q6;
            {var subQ0=sQuery(id+"F31.wireOp",EDGE,"E22.13.2");var subQ1=sQuery(id+"F31.wireOp",EDGE,"E22.12.0");var subQ2=makeQuery(id+"F31.imprint","INTERSECT",VERTEX,{"derivedFrom":[subQ1,subQ0]});Q6=makeQuery(id+"F31.imprint","IMPRINT",FACE,{"disambiguationData":[TD([[makeQuery(id+"F31.imprint","IMPRINT",EDGE,{"disambiguationData":[TD([[subQ2,-1.0]])],"derivedFrom":subQ1}),1.0]])]});}
            var Q7;
            {var subQ0=sQuery(id+"F31.wireOp",EDGE,"E22.14.2");var subQ1=sQuery(id+"F31.wireOp",EDGE,"E22.13.0");var subQ2=makeQuery(id+"F31.imprint","INTERSECT",VERTEX,{"derivedFrom":[subQ1,subQ0]});Q7=makeQuery(id+"F31.imprint","IMPRINT",FACE,{"disambiguationData":[TD([[makeQuery(id+"F31.imprint","IMPRINT",EDGE,{"disambiguationData":[TD([[subQ2,-1.0]])],"derivedFrom":subQ1}),1.0]])]});}
            var Q8;
            {var subQ0=sQuery(id+"F31.wireOp",EDGE,"E22.23.2");var subQ1=sQuery(id+"F31.wireOp",EDGE,"E22.22.0");var subQ2=makeQuery(id+"F31.imprint","INTERSECT",VERTEX,{"derivedFrom":[subQ1,subQ0]});Q8=makeQuery(id+"F31.imprint","IMPRINT",FACE,{"disambiguationData":[TD([[makeQuery(id+"F31.imprint","IMPRINT",EDGE,{"disambiguationData":[TD([[subQ2,-1.0]])],"derivedFrom":subQ1}),1.0]])]});}
            var Q9;
            {var subQ0=sQuery(id+"F31.wireOp",EDGE,"E22.22.2");var subQ1=sQuery(id+"F31.wireOp",EDGE,"E22.21.0");var subQ2=makeQuery(id+"F31.imprint","INTERSECT",VERTEX,{"derivedFrom":[subQ1,subQ0]});Q9=makeQuery(id+"F31.imprint","IMPRINT",FACE,{"disambiguationData":[TD([[makeQuery(id+"F31.imprint","IMPRINT",EDGE,{"disambiguationData":[TD([[subQ2,-1.0]])],"derivedFrom":subQ1}),1.0]])]});}
            var Q10;
            {var subQ0=sQuery(id+"F31.wireOp",EDGE,"E22.21.2");var subQ1=sQuery(id+"F31.wireOp",EDGE,"E22.20.0");var subQ2=makeQuery(id+"F31.imprint","INTERSECT",VERTEX,{"derivedFrom":[subQ1,subQ0]});Q10=makeQuery(id+"F31.imprint","IMPRINT",FACE,{"disambiguationData":[TD([[makeQuery(id+"F31.imprint","IMPRINT",EDGE,{"disambiguationData":[TD([[subQ2,-1.0]])],"derivedFrom":subQ1}),1.0]])]});}
            var Q11;
            {var subQ0=sQuery(id+"F31.wireOp",EDGE,"E22.20.2");var subQ1=sQuery(id+"F31.wireOp",EDGE,"E22.19.0");var subQ2=makeQuery(id+"F31.imprint","INTERSECT",VERTEX,{"derivedFrom":[subQ1,subQ0]});Q11=makeQuery(id+"F31.imprint","IMPRINT",FACE,{"disambiguationData":[TD([[makeQuery(id+"F31.imprint","IMPRINT",EDGE,{"disambiguationData":[TD([[subQ2,-1.0]])],"derivedFrom":subQ1}),1.0]])]});}
            var Q12;
            {var subQ0=sQuery(id+"F31.wireOp",EDGE,"E22.19.2");var subQ1=sQuery(id+"F31.wireOp",EDGE,"E22.18.0");var subQ2=makeQuery(id+"F31.imprint","INTERSECT",VERTEX,{"derivedFrom":[subQ1,subQ0]});Q12=makeQuery(id+"F31.imprint","IMPRINT",FACE,{"disambiguationData":[TD([[makeQuery(id+"F31.imprint","IMPRINT",EDGE,{"disambiguationData":[TD([[subQ2,-1.0]])],"derivedFrom":subQ1}),1.0]])]});}
            var Q13;
            {var subQ0=sQuery(id+"F31.wireOp",EDGE,"E22.18.2");var subQ1=sQuery(id+"F31.wireOp",EDGE,"E22.17.0");var subQ2=makeQuery(id+"F31.imprint","INTERSECT",VERTEX,{"derivedFrom":[subQ1,subQ0]});Q13=makeQuery(id+"F31.imprint","IMPRINT",FACE,{"disambiguationData":[TD([[makeQuery(id+"F31.imprint","IMPRINT",EDGE,{"disambiguationData":[TD([[subQ2,-1.0]])],"derivedFrom":subQ1}),1.0]])]});}
            var Q14;
            {var subQ0=sQuery(id+"F31.wireOp",EDGE,"E22.17.2");var subQ1=sQuery(id+"F31.wireOp",EDGE,"E22.16.0");var subQ2=makeQuery(id+"F31.imprint","INTERSECT",VERTEX,{"derivedFrom":[subQ1,subQ0]});Q14=makeQuery(id+"F31.imprint","IMPRINT",FACE,{"disambiguationData":[TD([[makeQuery(id+"F31.imprint","IMPRINT",EDGE,{"disambiguationData":[TD([[subQ2,-1.0]])],"derivedFrom":subQ1}),1.0]])]});}
            var Q15;
            {var subQ0=sQuery(id+"F31.wireOp",EDGE,"E22.16.2");var subQ1=sQuery(id+"F31.wireOp",EDGE,"E22.15.0");var subQ2=makeQuery(id+"F31.imprint","INTERSECT",VERTEX,{"derivedFrom":[subQ1,subQ0]});Q15=makeQuery(id+"F31.imprint","IMPRINT",FACE,{"disambiguationData":[TD([[makeQuery(id+"F31.imprint","IMPRINT",EDGE,{"disambiguationData":[TD([[subQ2,-1.0]])],"derivedFrom":subQ1}),1.0]])]});}
            var Q16;
            {var subQ0=sQuery(id+"F31.wireOp",EDGE,"E22.15.2");var subQ1=sQuery(id+"F31.wireOp",EDGE,"E22.14.0");var subQ2=makeQuery(id+"F31.imprint","INTERSECT",VERTEX,{"derivedFrom":[subQ1,subQ0]});Q16=makeQuery(id+"F31.imprint","IMPRINT",FACE,{"disambiguationData":[TD([[makeQuery(id+"F31.imprint","IMPRINT",EDGE,{"disambiguationData":[TD([[subQ2,-1.0]])],"derivedFrom":subQ1}),1.0]])]});}
            extrude(context, id + "F32", {"entities" : qUnion([Q0, Q1, Q2, Q3, Q4, Q5, Q6, Q7, Q8, Q9, Q10, Q11, Q12, Q13, Q14, Q15, Q16]), "operationType" : NewBodyOperationType.REMOVE, "oppositeDirection" : true, "depth" : 5 * mm});
        }
        {
            var Q0;
            {var subQ0=sQuery(id+"F6.wireOp",EDGE,"E3.2");Q0=makeQuery(id+"F8.boolean.opBoolean","MERGE",FACE,{"derivedFrom":[makeQuery(id+"F7.boolean.opBoolean","COPY",FACE,{"derivedFrom":makeQuery(id+"F7.opExtrude","SWEPT_FACE",FACE,{"disambiguationData":[OSD([subQ0])]})}),makeQuery(id+"F8.opExtrude","SWEPT_FACE",FACE,{"disambiguationData":[OSD([subQ0])]})]});}
            var sketch = newSketch(context, id + "F33", { "sketchPlane" : qUnion([Q0])});
            skCircle(sketch, "E23", {"center": v(3.68, 12.73) * mm, "radius": 2.04 * mm});
            skPoint(sketch, "E23.centerSnap0", {"position": v(10.5, 12.73) * mm});
            skSolve(sketch);
        }
        {
            var Q0;
            Q0 = qSketchRegion(id + "F33", true);
            extrude(context, id + "F34", {"entities" : qUnion([Q0]), "operationType" : NewBodyOperationType.ADD, "depth" : 5 * mm});
        }
        {
            var Q0;
            Q0=makeQuery(id+"F25.boolean.opBoolean","COPY",FACE,{"derivedFrom":makeQuery(id+"F25.opExtrude","CAP_FACE",FACE,{"disambiguationData":[OSD([sQuery(id+"F24.wireOp",EDGE,"E15")])],"isStart":false})});
            var sketch = newSketch(context, id + "F35", { "sketchPlane" : qUnion([Q0])});
            skLineSegment(sketch, "E24.bottom", {"start": v(0.7, -5) * mm, "end": v(0, -5) * mm});
            skLineSegment(sketch, "E24.top", {"start": v(0.7, -2.88) * mm, "end": v(0, -2.88) * mm});
            skLineSegment(sketch, "E24.left", {"start": v(0.7, -5) * mm, "end": v(0.7, -2.88) * mm});
            skLineSegment(sketch, "E24.right", {"start": v(0, -5) * mm, "end": v(0, -2.88) * mm});
            skLineSegment(sketch, "E25.1.0", {"start": v(7.64, 2.64) * mm, "end": v(5.53, 2.64) * mm});
            skLineSegment(sketch, "E25.1.1", {"start": v(7.64, 3.35) * mm, "end": v(5.53, 3.35) * mm});
            skLineSegment(sketch, "E25.1.2", {"start": v(7.64, 3.35) * mm, "end": v(7.64, 2.64) * mm});
            skLineSegment(sketch, "E25.1.3", {"start": v(5.53, 3.35) * mm, "end": v(5.53, 2.64) * mm});
            skLineSegment(sketch, "E25.2.0", {"start": v(0, 10.29) * mm, "end": v(0, 8.17) * mm});
            skLineSegment(sketch, "E25.2.1", {"start": v(-0.7, 10.29) * mm, "end": v(-0.7, 8.17) * mm});
            skLineSegment(sketch, "E25.2.2", {"start": v(-0.7, 10.29) * mm, "end": v(0, 10.29) * mm});
            skLineSegment(sketch, "E25.2.3", {"start": v(-0.7, 8.17) * mm, "end": v(0, 8.17) * mm});
            skLineSegment(sketch, "E25.3.0", {"start": v(-7.64, 2.64) * mm, "end": v(-5.53, 2.64) * mm});
            skLineSegment(sketch, "E25.3.1", {"start": v(-7.64, 1.94) * mm, "end": v(-5.53, 1.94) * mm});
            skLineSegment(sketch, "E25.3.2", {"start": v(-7.64, 1.94) * mm, "end": v(-7.64, 2.64) * mm});
            skLineSegment(sketch, "E25.3.3", {"start": v(-5.53, 1.94) * mm, "end": v(-5.53, 2.64) * mm});
            skPoint(sketch, "E25.center", {"position": v(0, 2.64) * mm});
            skSolve(sketch);
        }
        {
            var Q0;
            Q0=makeQuery(id+"F35.imprint","IMPRINT",FACE,{"disambiguationData":[TD([[makeQuery(id+"F35.imprint","IMPRINT",EDGE,{"derivedFrom":sQuery(id+"F35.wireOp",EDGE,"E25.2.0")}),-1.0]])]});
            var Q1;
            Q1=makeQuery(id+"F35.imprint","IMPRINT",FACE,{"disambiguationData":[TD([[makeQuery(id+"F35.imprint","IMPRINT",EDGE,{"derivedFrom":sQuery(id+"F35.wireOp",EDGE,"E25.3.0")}),-1.0]])]});
            var Q2;
            Q2=makeQuery(id+"F35.imprint","IMPRINT",FACE,{"disambiguationData":[TD([[makeQuery(id+"F35.imprint","IMPRINT",EDGE,{"derivedFrom":sQuery(id+"F35.wireOp",EDGE,"E24.bottom")}),-1.0]])]});
            var Q3;
            Q3=makeQuery(id+"F35.imprint","IMPRINT",FACE,{"disambiguationData":[TD([[makeQuery(id+"F35.imprint","IMPRINT",EDGE,{"derivedFrom":sQuery(id+"F35.wireOp",EDGE,"E25.1.0")}),-1.0]])]});
            extrude(context, id + "F36", {"entities" : qUnion([Q0, Q1, Q2, Q3]), "operationType" : NewBodyOperationType.ADD, "depth" : 5 * mm});
        }
        {
            var Q0;
            Q0=makeQuery(id+"F30.boolean.opBoolean","COPY",FACE,{"derivedFrom":makeQuery(id+"F30.opExtrude","CAP_FACE",FACE,{"disambiguationData":[OSD([sQuery(id+"F22.wireOp",EDGE,"E14"),sQuery(id+"F29.wireOp",EDGE,"E17")])],"isStart":false})});
            var sketch = newSketch(context, id + "F37", { "sketchPlane" : qUnion([Q0])});
            skLineSegment(sketch, "E26", {"start": v(1.46, -10.6) * mm, "end": v(1.46, -6.03) * mm});
            skLineSegment(sketch, "E27", {"start": v(1.46, -6.03) * mm, "end": v(-1.1, -6.03) * mm});
            skLineSegment(sketch, "E28", {"start": v(-1.1, -6.03) * mm, "end": v(-1.1, -10.65) * mm});
            skLineSegment(sketch, "E29", {"start": v(-1.1, -10.65) * mm, "end": v(1.46, -10.6) * mm});
            skLineSegment(sketch, "E30.1.0", {"start": v(13.3, 1.55) * mm, "end": v(13.24, 4.1) * mm});
            skLineSegment(sketch, "E30.1.1", {"start": v(8.67, 1.55) * mm, "end": v(13.3, 1.55) * mm});
            skLineSegment(sketch, "E30.1.2", {"start": v(8.67, 4.1) * mm, "end": v(8.67, 1.55) * mm});
            skLineSegment(sketch, "E30.1.3", {"start": v(13.24, 4.1) * mm, "end": v(8.67, 4.1) * mm});
            skLineSegment(sketch, "E30.2.0", {"start": v(1.1, 15.94) * mm, "end": v(-1.46, 15.89) * mm});
            skLineSegment(sketch, "E30.2.1", {"start": v(1.1, 11.32) * mm, "end": v(1.1, 15.94) * mm});
            skLineSegment(sketch, "E30.2.2", {"start": v(-1.46, 11.32) * mm, "end": v(1.1, 11.32) * mm});
            skLineSegment(sketch, "E30.2.3", {"start": v(-1.46, 15.89) * mm, "end": v(-1.46, 11.32) * mm});
            skLineSegment(sketch, "E30.3.0", {"start": v(-13.3, 3.74) * mm, "end": v(-13.24, 1.19) * mm});
            skLineSegment(sketch, "E30.3.1", {"start": v(-8.67, 3.74) * mm, "end": v(-13.3, 3.74) * mm});
            skLineSegment(sketch, "E30.3.2", {"start": v(-8.67, 1.19) * mm, "end": v(-8.67, 3.74) * mm});
            skLineSegment(sketch, "E30.3.3", {"start": v(-13.24, 1.19) * mm, "end": v(-8.67, 1.19) * mm});
            skPoint(sketch, "E30.center", {"position": v(0, 2.64) * mm});
            skSolve(sketch);
        }
        {
            var Q0;
            Q0=makeQuery(id+"F37.imprint","IMPRINT",FACE,{"disambiguationData":[TD([[makeQuery(id+"F37.imprint","IMPRINT",EDGE,{"derivedFrom":sQuery(id+"F37.wireOp",EDGE,"E30.1.0")}),1.0]])]});
            var Q1;
            Q1=makeQuery(id+"F37.imprint","IMPRINT",FACE,{"disambiguationData":[TD([[makeQuery(id+"F37.imprint","IMPRINT",EDGE,{"derivedFrom":sQuery(id+"F37.wireOp",EDGE,"E26")}),1.0]])]});
            var Q2;
            Q2=makeQuery(id+"F37.imprint","IMPRINT",FACE,{"disambiguationData":[TD([[makeQuery(id+"F37.imprint","IMPRINT",EDGE,{"derivedFrom":sQuery(id+"F37.wireOp",EDGE,"E30.3.0")}),1.0]])]});
            var Q3;
            Q3=makeQuery(id+"F37.imprint","IMPRINT",FACE,{"disambiguationData":[TD([[makeQuery(id+"F37.imprint","IMPRINT",EDGE,{"derivedFrom":sQuery(id+"F37.wireOp",EDGE,"E30.2.0")}),1.0]])]});
            extrude(context, id + "F38", {"entities" : qUnion([Q0, Q1, Q2, Q3]), "operationType" : NewBodyOperationType.ADD, "depth" : 3 * mm});
        }
        {
            var Q0;
            Q0=makeQuery(id+"F16.boolean.opBoolean","COPY",FACE,{"derivedFrom":makeQuery(id+"F16.opExtrude","CAP_FACE",FACE,{"disambiguationData":[OSD([sQuery(id+"F15.wireOp",EDGE,"E7")])],"isStart":false})});
            var sketch = newSketch(context, id + "F39", { "sketchPlane" : qUnion([Q0])});
            skLineSegment(sketch, "E31", {"start": v(-0.51, 4.3) * mm, "end": v(0.75, 4.3) * mm});
            skLineSegment(sketch, "E32", {"start": v(0.75, 4.3) * mm, "end": v(0.75, 2.64) * mm});
            skLineSegment(sketch, "E33", {"start": v(0.75, 2.64) * mm, "end": v(-0.49, 2.64) * mm});
            skLineSegment(sketch, "E34", {"start": v(-0.49, 2.64) * mm, "end": v(-0.51, 4.3) * mm});
            skLineSegment(sketch, "E35.1.0", {"start": v(-5.9, -2.51) * mm, "end": v(-5.9, -3.74) * mm});
            skLineSegment(sketch, "E35.1.1", {"start": v(-7.55, -2.51) * mm, "end": v(-5.9, -2.51) * mm});
            skLineSegment(sketch, "E35.1.2", {"start": v(-7.55, -3.77) * mm, "end": v(-7.55, -2.51) * mm});
            skLineSegment(sketch, "E35.1.3", {"start": v(-5.9, -3.74) * mm, "end": v(-7.55, -3.77) * mm});
            skLineSegment(sketch, "E35.2.0", {"start": v(-0.75, -9.15) * mm, "end": v(0.49, -9.15) * mm});
            skLineSegment(sketch, "E35.2.1", {"start": v(-0.75, -10.8) * mm, "end": v(-0.75, -9.15) * mm});
            skLineSegment(sketch, "E35.2.2", {"start": v(0.51, -10.8) * mm, "end": v(-0.75, -10.8) * mm});
            skLineSegment(sketch, "E35.2.3", {"start": v(0.49, -9.15) * mm, "end": v(0.51, -10.8) * mm});
            skLineSegment(sketch, "E35.3.0", {"start": v(5.9, -4) * mm, "end": v(5.9, -2.77) * mm});
            skLineSegment(sketch, "E35.3.1", {"start": v(7.55, -4) * mm, "end": v(5.9, -4) * mm});
            skLineSegment(sketch, "E35.3.2", {"start": v(7.55, -2.74) * mm, "end": v(7.55, -4) * mm});
            skLineSegment(sketch, "E35.3.3", {"start": v(5.9, -2.77) * mm, "end": v(7.55, -2.74) * mm});
            skPoint(sketch, "E35.center", {"position": v(0, -3.26) * mm});
            skSolve(sketch);
        }
        {
            var Q0;
            Q0=makeQuery(id+"F39.imprint","IMPRINT",FACE,{"disambiguationData":[TD([[makeQuery(id+"F39.imprint","IMPRINT",EDGE,{"derivedFrom":sQuery(id+"F39.wireOp",EDGE,"E35.3.0")}),-1.0]])]});
            var Q1;
            Q1=makeQuery(id+"F39.imprint","IMPRINT",FACE,{"disambiguationData":[TD([[makeQuery(id+"F39.imprint","IMPRINT",EDGE,{"derivedFrom":sQuery(id+"F39.wireOp",EDGE,"E35.2.0")}),-1.0]])]});
            var Q2;
            Q2=makeQuery(id+"F39.imprint","IMPRINT",FACE,{"disambiguationData":[TD([[makeQuery(id+"F39.imprint","IMPRINT",EDGE,{"derivedFrom":sQuery(id+"F39.wireOp",EDGE,"E31")}),-1.0]])]});
            var Q3;
            Q3=makeQuery(id+"F39.imprint","IMPRINT",FACE,{"disambiguationData":[TD([[makeQuery(id+"F39.imprint","IMPRINT",EDGE,{"derivedFrom":sQuery(id+"F39.wireOp",EDGE,"E35.1.0")}),-1.0]])]});
            extrude(context, id + "F40", {"entities" : qUnion([Q0, Q1, Q2, Q3]), "operationType" : NewBodyOperationType.ADD, "depth" : 5 * mm});
        }
    });
